# Revit family: STH8141_27_30
name_source: partatom
category: Luminárias
units: mm (PartAtom-declared; Revit-internal decimal feet)

## family parameters
Com base no plano de trabalho = Não
Compartilhado = Não
Corte com vazios quando carregada = Não
Cota do conector redondo = Utilizar diâmetro
Fonte luminosa = Sim
Manter orientação da anotação = Não
Ponto de cálculo do ambiente = Não
Sempre na vertical = Sim
Tipo de parte = Normal

## types (2) — shared parameters
Altura = 0.06 m
Comprimento = 0.02 m
Cromado = Cromado
Dimerização = Não dimerizável
Fabricante = Stella
Filtro de cor = 16777215
Fluxo Luminoso = 325 lm
Grau de proteção (IP) = IP20
IRC (Índice de reprodução de cores) = >80
Largura = 0.01 m
Modelo = Bipino G9
Potência = 4 W
Tensão Elétrica = 127V
Troca de temperatura da cor de lâmpada com esmaecimento = <Nenhum>
URL = https://stella.com.br
Ângulo de Abertura = 300°
Ângulo de inclinação = 90.00°
zero-valued in all types: Elevação padrão

## per-type parameters (varying)
| type | Arquivo de rede fotométrica | Estrutura | Referência | Temperatura da cor (K) |
| STH8141/27 - 127V - 2700K - 325lm - 300° | STELLA - STH8141-27 - BIPINO G9 4W.ies | Luminoso - 2700K | STH8141/27 - 127V | 2700 K |
| STH8141/30 - 127V - 3000K - 325lm - 300° | STELLA - STH8141-30 - BIPINO G9 4W.ies | Luminoso - 3000K | STH8141/30 - 127V | 3000 K |
